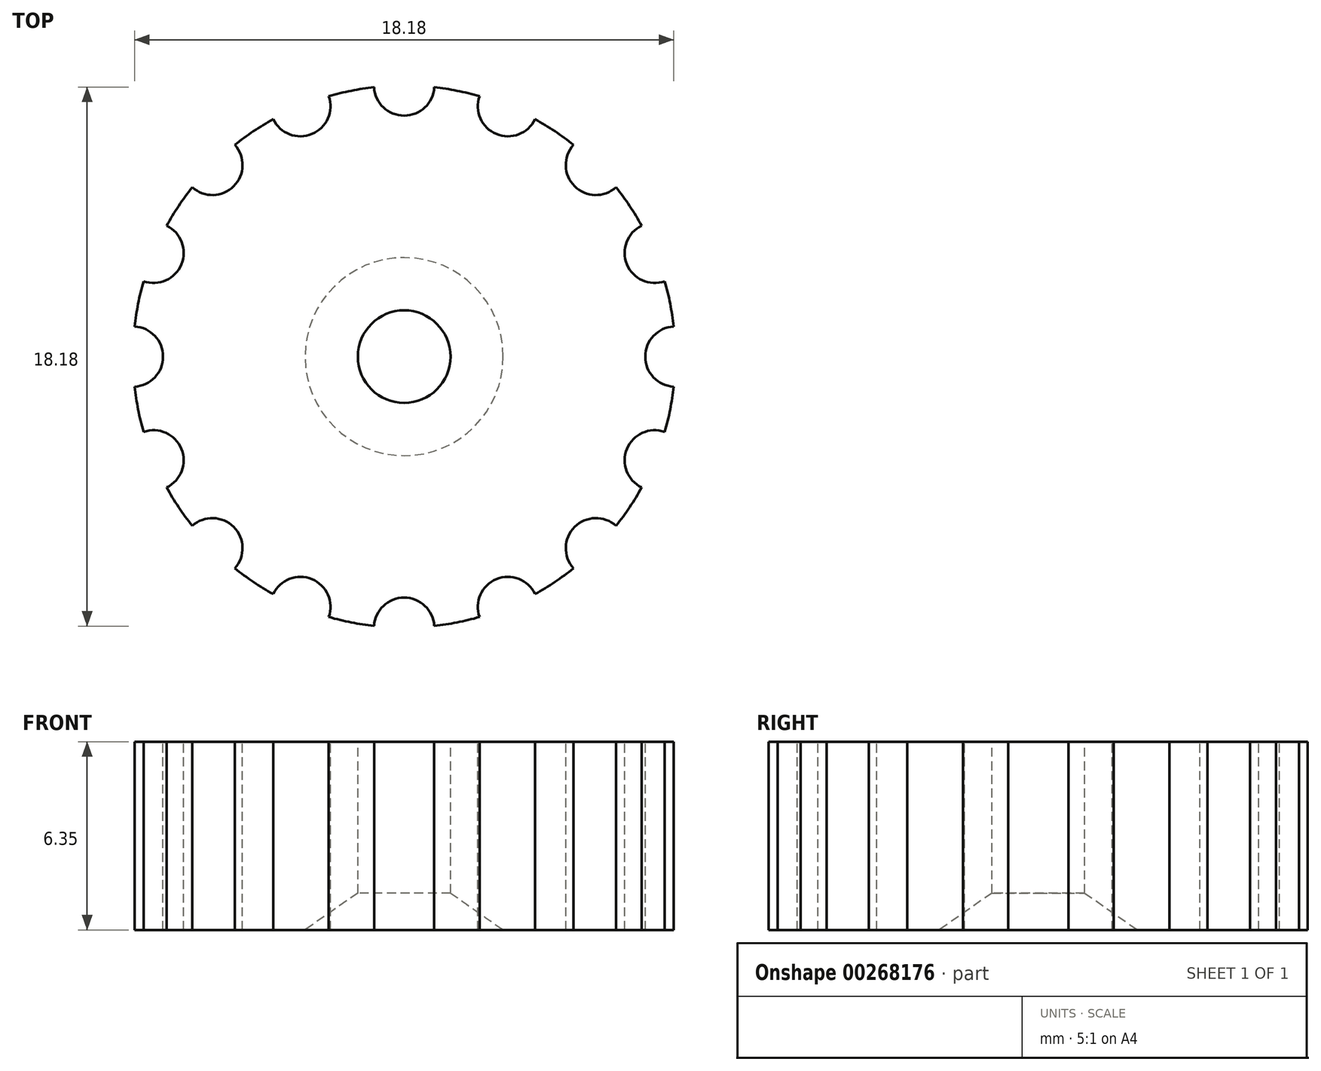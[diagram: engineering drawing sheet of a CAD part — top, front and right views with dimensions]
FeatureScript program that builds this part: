
annotation { "Feature Type Name" : "Feature", "Feature Type Description" : "" }
export const myFeature = defineFeature(function(context is Context, id is Id, definition is map)
    precondition{}
    {
        {
            var Q0;
            Q0=qCreatedBy(makeId("Top.planeOp"),FACE);
            var sketch = newSketch(context, id + "F0", { "sketchPlane" : qUnion([Q0])});
            skCircle(sketch, "E0", {"center": v(0, 0) * mm, "radius": 9.14 * mm});
            skSolve(sketch);
        }
        {
            var Q0;
            Q0 = qSketchRegion(id + "F0", true);
            extrude(context, id + "F1", {"entities" : qUnion([Q0]), "depth" : 6.35 * mm});
        }
        {
            var Q0;
            Q0=makeQuery(id+"F1.opExtrude","CAP_FACE",FACE,{"disambiguationData":[OSD([sQuery(id+"F0.wireOp",EDGE,"E0")])],"isStart":false});
            var sketch = newSketch(context, id + "F2", { "sketchPlane" : qUnion([Q0])});
            skCircle(sketch, "E1", {"center": v(0, 0) * mm, "radius": 1.56 * mm});
            skSolve(sketch);
        }
        {
            var Q0;
            Q0=makeQuery(id+"F2.imprint","IMPRINT",FACE,{"disambiguationData":[TD([[makeQuery(id+"F2.imprint","IMPRINT",EDGE,{"derivedFrom":sQuery(id+"F2.wireOp",EDGE,"E1")}),1.0]])]});
            extrude(context, id + "F3", {"entities" : qUnion([Q0]), "operationType" : NewBodyOperationType.REMOVE, "endBound" : BoundingType.THROUGH_ALL, "oppositeDirection" : true, "depth" : 25.4 * mm});
        }
        {
            var Q0;
            Q0=makeQuery(id+"F3.boolean.opBoolean","INTERSECT",EDGE,{"derivedFrom":[makeQuery(id+"F1.opExtrude","CAP_FACE",FACE,{"disambiguationData":[OSD([sQuery(id+"F0.wireOp",EDGE,"E0")])],"isStart":true}),makeQuery(id+"F3.opExtrude","SWEPT_FACE",FACE,{"disambiguationData":[OSD([sQuery(id+"F2.wireOp",EDGE,"E1")])]})]});
            chamfer(context, id + "F4", {"entities" : qUnion([Q0]), "chamferType" : ChamferType.OFFSET_ANGLE, "width" : 1.78 * mm, "oppositeDirection" : false, "angle" : 35 * degree, "tangentPropagation" : true});
        }
        {
            var Q0;
            Q0=makeQuery(id+"F1.opExtrude","CAP_FACE",FACE,{"disambiguationData":[OSD([sQuery(id+"F0.wireOp",EDGE,"E0")])],"isStart":false});
            var sketch = newSketch(context, id + "F5", { "sketchPlane" : qUnion([Q0])});
            skLineSegment(sketch, "E2", {"start": v(0, 0) * mm, "end": v(0, 9.14) * mm});
            skCircle(sketch, "E3", {"center": v(0, 9.14) * mm, "radius": 1.02 * mm});
            skCircle(sketch, "E4.1.0", {"center": v(-3.5, 8.45) * mm, "radius": 1.02 * mm});
            skCircle(sketch, "E4.2.0", {"center": v(-6.47, 6.47) * mm, "radius": 1.02 * mm});
            skCircle(sketch, "E4.3.0", {"center": v(-8.45, 3.5) * mm, "radius": 1.02 * mm});
            skCircle(sketch, "E4.4.0", {"center": v(-9.14, 0) * mm, "radius": 1.02 * mm});
            skCircle(sketch, "E4.5.0", {"center": v(-8.45, -3.5) * mm, "radius": 1.02 * mm});
            skCircle(sketch, "E4.6.0", {"center": v(-6.47, -6.47) * mm, "radius": 1.02 * mm});
            skCircle(sketch, "E4.7.0", {"center": v(-3.5, -8.45) * mm, "radius": 1.02 * mm});
            skCircle(sketch, "E4.8.0", {"center": v(0, -9.14) * mm, "radius": 1.02 * mm});
            skCircle(sketch, "E4.9.0", {"center": v(3.5, -8.45) * mm, "radius": 1.02 * mm});
            skCircle(sketch, "E4.10.0", {"center": v(6.47, -6.47) * mm, "radius": 1.02 * mm});
            skCircle(sketch, "E4.11.0", {"center": v(8.45, -3.5) * mm, "radius": 1.02 * mm});
            skCircle(sketch, "E4.12.0", {"center": v(9.14, 0) * mm, "radius": 1.02 * mm});
            skCircle(sketch, "E4.13.0", {"center": v(8.45, 3.5) * mm, "radius": 1.02 * mm});
            skCircle(sketch, "E4.14.0", {"center": v(6.47, 6.47) * mm, "radius": 1.02 * mm});
            skCircle(sketch, "E4.15.0", {"center": v(3.5, 8.45) * mm, "radius": 1.02 * mm});
            skPoint(sketch, "E4.center", {"position": v(0, 0) * mm});
            skSolve(sketch);
        }
        {
            var Q0;
            Q0 = qSketchRegion(id + "F5", true);
            extrude(context, id + "F6", {"entities" : qUnion([Q0]), "operationType" : NewBodyOperationType.REMOVE, "endBound" : BoundingType.THROUGH_ALL, "oppositeDirection" : true, "depth" : 25.4 * mm});
        }
    });
